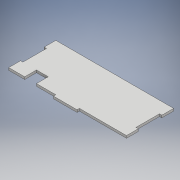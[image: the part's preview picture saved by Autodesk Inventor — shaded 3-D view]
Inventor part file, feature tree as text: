
AUTODESK INVENTOR PART (.ipt)
format: ipt  version: 2017 (Build 210142000, 142)  size: 114,688 bytes
history: native  units: mm
features: extrude x1, sketch x1
ambient origin geometry x8: Origin, YZ Plane, XZ Plane, XY Plane, X Axis, Y Axis, Z Axis, Center Point
bodies: Solid1 (feature_tree)
feature tree (2):
  extrude  "Extrusion1"  Depth=3.0mm TaperAngle=0.0deg
  sketch  "Sketch1"  dims[d10=150.0mm d11=60.0mm d12=3.0mm d13=15.0mm d14=3.0mm d15=30.0mm d16=30.0mm d17=3.0mm d18=3.0mm d19=15.0mm d20=3.0mm d21=0.0mm d22=1.0mm d23=1.0mm]
